# Revit family: Hager-Orion_Plus-IP65-D250-Cl.I-Steel_encl-630A-NoHosted-ES-es
name_source: partatom
category: Electrical Equipment
units: mm (PartAtom-declared; Revit-internal decimal feet)

## family parameters
Always vertical = Yes
Cut with Voids When Loaded = No
Panel Configuration = Two Columns, Circuits Across
Part Type = Panelboard
Room Calculation Point = No
Round Connector Dimension = Use Diameter
Shared = No
Work Plane-Based = Yes

## types (1)
- Montado superficial (escayola) IP65 A500 A650 P250  - FL120A
    Default Elevation = 1219 mm
    EF000003 - Tipo de montaje = EV000384 - Montado superficial (escayola)
    EF000007 - Color = EV000270 - Gris
    EF000008 - Anchura = 500 mm  [stored 1.64042 ft]
    EF000040 - Altura = 650 mm  [stored 2.13255 ft]
    EF000049 - Profundidad = 250 mm  [stored 0.82021 ft]
    EF000116 - Número RAL = 7035
    EF000118 - Con placa de montaje = No
    EF000218 - Profundidad de instalación = 0 mm  [stored 0 ft]
    EF000266 - Número de filas = 4
    EF000339 - Tipo de cubierta = EV001012 - Cubrir
    EF000437 - Número de entradas de conductos de cables = 2
    EF001088 - Posibilidad de extensión = Yes
    EF001131 - Profundidad interna = 250 mm  [stored 0.82021 ft]
    EF001596 - Material de la carcasa = EV000179 - Acero
    EF001613 - Integridad del circuito = EV000494 - Ninguno
    EF002950 - Anchura de unidades de división = 22
    EF003532 - Adecuado para uso en exteriores = No
    EF004293 - Resistencia al impacto (IK) = EV008784 - IK10
    EF004427 - Número de módulos = 88
    EF004464 - Tipo de puerta = EV002646 - Único
    EF005474 - Grado de protección (IP) = EV006421 - IP65
    EF006244 - Tapa/puerta transparente = No
    EF006306 - Con cierre = Yes
    EF007800 - Adecuado para la protección contra rayos = No
    EF008873 - Corriente nominal (In) = 630 A
    EF009170 - Espesor del material de la caja = 2 mm  [stored 0.00656168 ft]
    EF009171 - Espesor puerta/tapa = 2 mm  [stored 0.00656168 ft]
    EF009212 - Versión de la cubierta = EV000116 - Cerrado
    EF009554 - Número de aberturas para placas-brida = 2
    EF015940 - Tapa con alivio de sobrepresión = No
    HG000002 - Con puerta o tapa = Yes
    HG000003 - Gama = Orion Plus
    HG000004 - Referencia del fabricante = FL120A
    HG000006 - Empotrado = No
    HG000009 - Puerta batiente doble = No
    HG000010 - Puertas asimétricas = No
    HG000023 - Caja de doble sección = No
    HG000024 - Altura de la sección inferior = 600 mm
    HG000026 - Instalación en suelo = No
    HG000027 - Altura de zócalo = 0 mm  [stored 0 ft]
    Manufacturer = Hager
    Type Comments = Orion Plus

note: [stored X ft] marks values corroborated as IEEE doubles in the binary element streams (Revit-internal decimal feet)

## geometry (parser evidence)
native form markers: Blend x4, Sweep x10
no freeform markers — native parametric forms only
